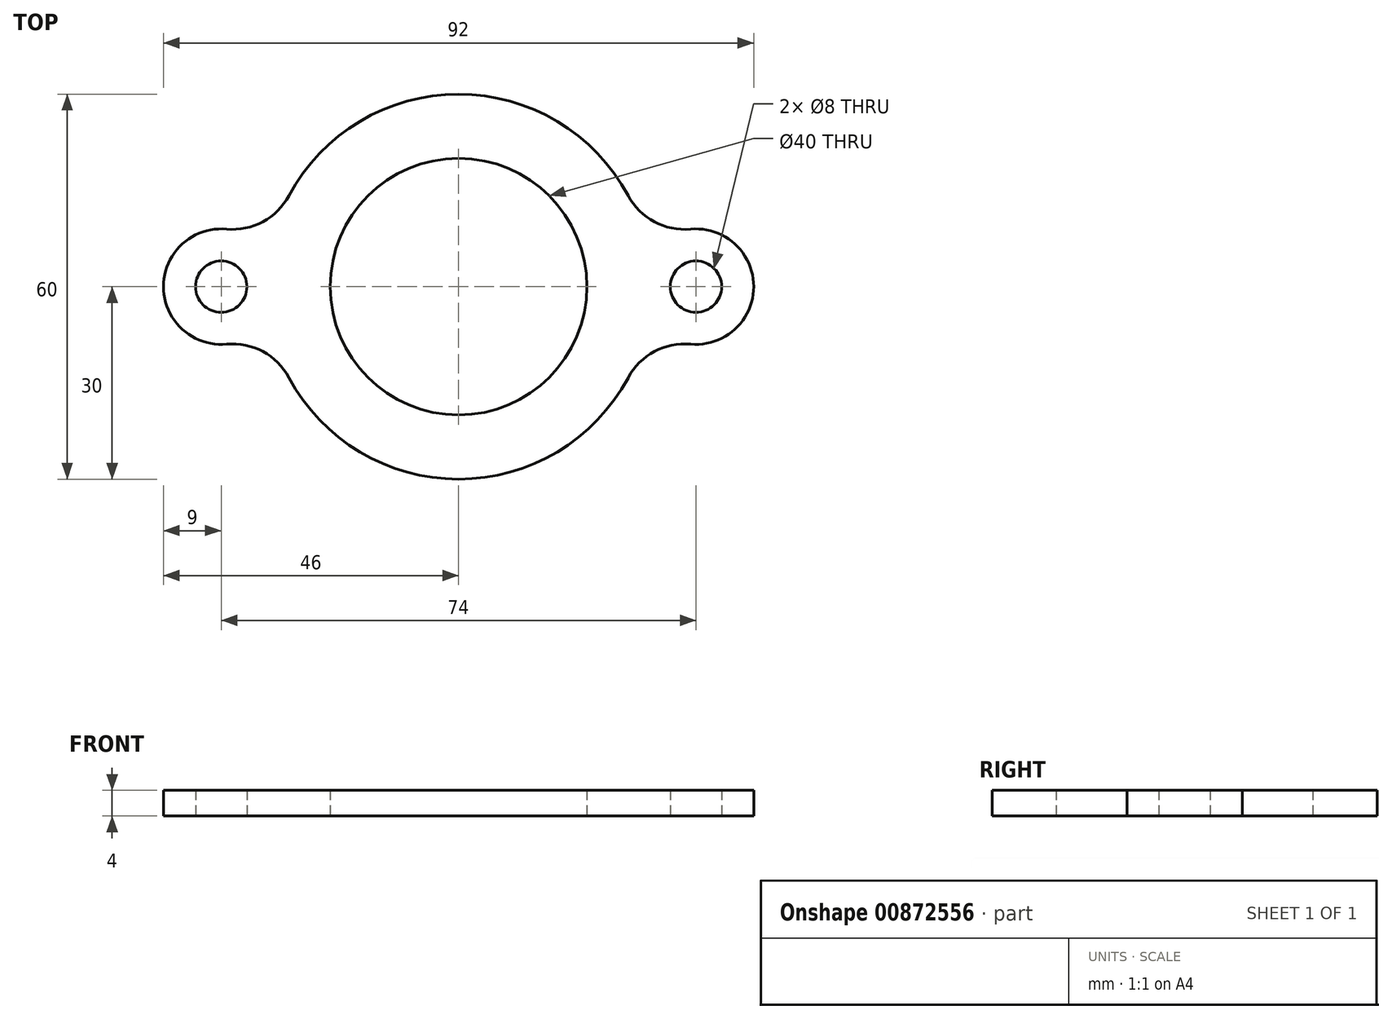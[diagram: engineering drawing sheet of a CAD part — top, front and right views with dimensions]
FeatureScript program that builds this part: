
annotation { "Feature Type Name" : "Feature", "Feature Type Description" : "" }
export const myFeature = defineFeature(function(context is Context, id is Id, definition is map)
    precondition{}
    {
        {
            var Q0;
            Q0=qCreatedBy(makeId("Top.planeOp"),FACE);
            var sketch = newSketch(context, id + "F0", { "sketchPlane" : qUnion([Q0])});
            skCircle(sketch, "E0", {"center": v(0, 0) * mm, "radius": 20 * mm});
            skLineSegment(sketch, "E1", {"start": v(0, 0) * mm, "end": v(-37, 0) * mm, "construction": true});
            skLineSegment(sketch, "E2", {"start": v(0, 0) * mm, "end": v(37, 0) * mm, "construction": true});
            skCircle(sketch, "E3", {"center": v(-37, 0) * mm, "radius": 4 * mm});
            skCircle(sketch, "E4", {"center": v(37, 0) * mm, "radius": 4 * mm});
            skArc(sketch, "E5.0", {"start": v(-26.43, -14.19) * mm, "mid": v(0, -30) * mm, "end": v(26.43, -14.19) * mm});
            skArc(sketch, "E6.0", {"start": v(-36.17, 8.96) * mm, "mid": v(-46, 0) * mm, "end": v(-36.17, -8.96) * mm});
            skArc(sketch, "E7.0", {"start": v(36.17, -8.96) * mm, "mid": v(46, 0) * mm, "end": v(36.17, 8.96) * mm});
            skArc(sketch, "E8.trimOffspring", {"start": v(26.43, 14.19) * mm, "mid": v(0, 30) * mm, "end": v(-26.43, 14.19) * mm});
            skPoint(sketch, "E9.visualSharp", {"position": v(29.57, -5.08) * mm});
            skArc(sketch, "E9.filletArc", {"start": v(36.17, -8.96) * mm, "mid": v(30.51, -10.1) * mm, "end": v(26.43, -14.19) * mm});
            skPoint(sketch, "E10.visualSharp", {"position": v(29.57, 5.08) * mm});
            skArc(sketch, "E10.filletArc", {"start": v(26.43, 14.19) * mm, "mid": v(30.51, 10.1) * mm, "end": v(36.17, 8.96) * mm});
            skPoint(sketch, "E11.visualSharp", {"position": v(-29.57, 5.08) * mm});
            skArc(sketch, "E11.filletArc", {"start": v(-36.17, 8.96) * mm, "mid": v(-30.51, 10.1) * mm, "end": v(-26.43, 14.19) * mm});
            skPoint(sketch, "E12.visualSharp", {"position": v(-29.57, -5.08) * mm});
            skArc(sketch, "E12.filletArc", {"start": v(-26.43, -14.19) * mm, "mid": v(-30.51, -10.1) * mm, "end": v(-36.17, -8.96) * mm});
            skSolve(sketch);
        }
        {
            var Q0;
            Q0=makeQuery(id+"F0.imprint","IMPRINT",FACE,{"disambiguationData":[TD([[makeQuery(id+"F0.imprint","IMPRINT",EDGE,{"derivedFrom":sQuery(id+"F0.wireOp",EDGE,"E0")}),-1.0]])]});
            extrude(context, id + "F1", {"entities" : qUnion([Q0]), "depth" : 4 * mm, "offsetDistance" : 25 * mm});
        }
    });
